# Revit family: E-32
name_source: partatom
category: Aparatos sanitarios
units: mm (PartAtom-declared; Revit-internal decimal feet)

## family parameters
Compartido = No
Corte con vacíos al cargar = No
Cota de conector redondo = Diámetro de uso
Número OmniClass = 23.45.00.00
Punto de cálculo de habitación = No
Se basa en plano de trabajo = No
Siempre vertical = Sí
Tipo de pieza = Normal
Título OmniClass = Sanitary, Laundry, and Cleaning Equipment

## types (1)
- E-32
    Brass Chromed = Brass Chromed
    Comentarios de tipo = Sinlge Control Kitchen Faucets
    Conexión AC = Sí
    Conexión AF = Sí
    Descripción = Single Control Kitchen Sink Faucet Nuva
    Documentation = http://www.helvex.com.mx
    Elevación por defecto = 0"
    Fabricante = Helvex
    Features = Ceramic Cartridge
    Inlet Threads = 1/2" - 14 Npsm
    Max. Working Pressure = 85.3 psi
    Min. Working Pressure = 8.5 psi
    Modelo = E-32
    Niquel Duravex = Niquel Duravex
    Satin = Satin
    Total Height = 12"
    Total Length = 10"
    URL = http://www.helvex.com.mx
    Ébano = Ébano

## geometry (parser evidence)
native form markers: Sweep x3
no freeform markers — native parametric forms only
